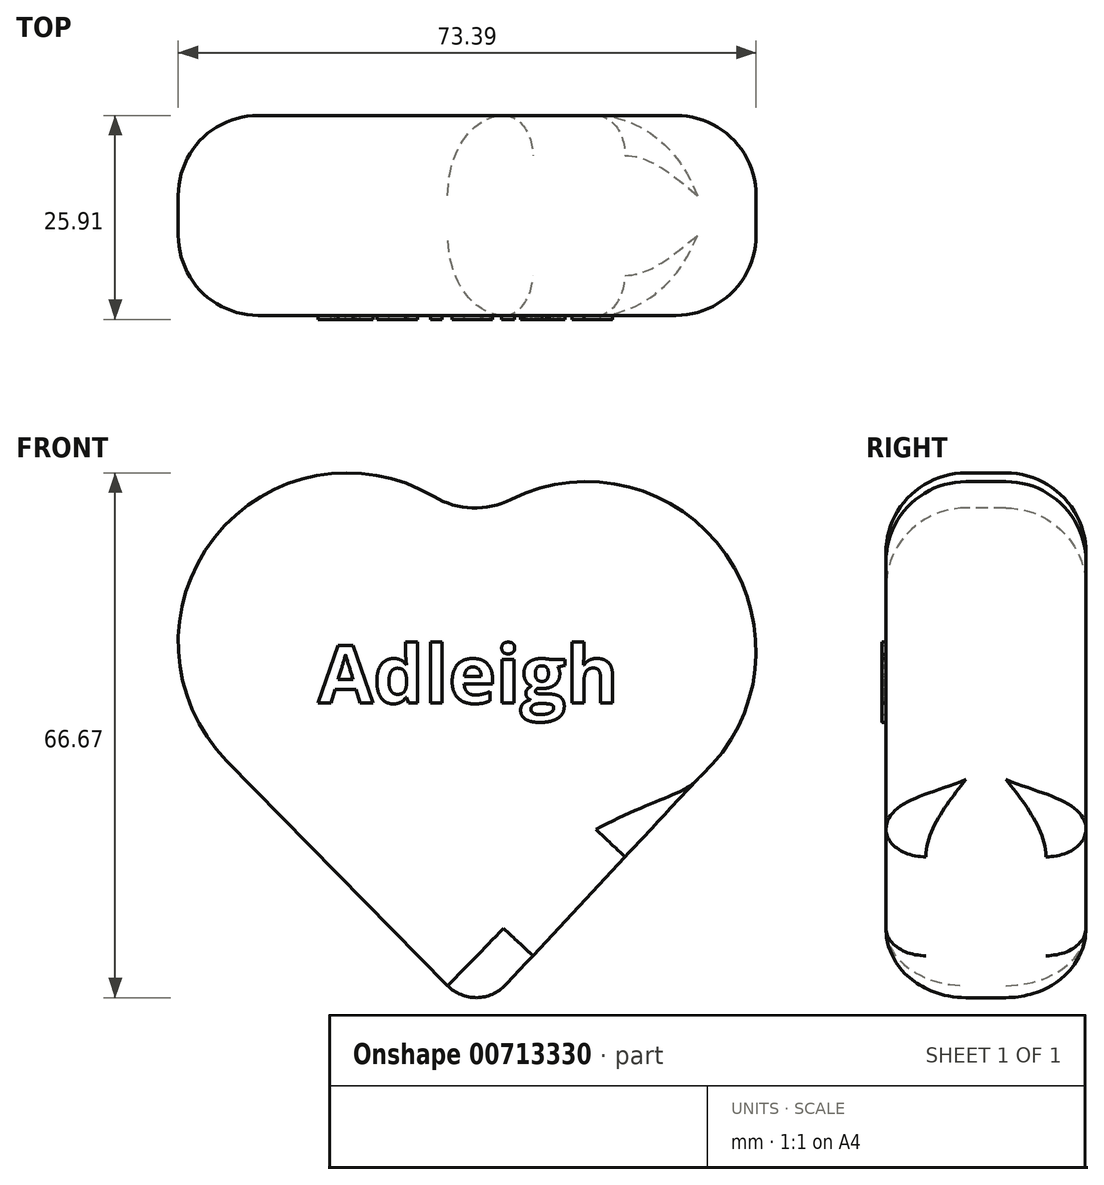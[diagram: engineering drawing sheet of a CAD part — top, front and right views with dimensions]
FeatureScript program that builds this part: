
annotation { "Feature Type Name" : "Feature", "Feature Type Description" : "" }
export const myFeature = defineFeature(function(context is Context, id is Id, definition is map)
    precondition{}
    {
        {
            var Q0;
            Q0=qCreatedBy(makeId("Front.planeOp"),FACE);
            var sketch = newSketch(context, id + "F0", { "sketchPlane" : qUnion([Q0])});
            skArc(sketch, "E0", {"start": v(-28.69, 48.9) * mm, "mid": v(-59.42, 50.26) * mm, "end": v(-60.06, 19.5) * mm});
            skArc(sketch, "E1", {"start": v(0, 17.42) * mm, "mid": v(1.36, 48.15) * mm, "end": v(-29.4, 48.8) * mm});
            skLineSegment(sketch, "E2", {"start": v(-60.06, 19.5) * mm, "end": v(-28.28, -12.86) * mm});
            skLineSegment(sketch, "E3", {"start": v(-28.28, -12.86) * mm, "end": v(0, 17.42) * mm});
            skSolve(sketch);
        }
        {
            var Q0;
            Q0 = qSketchRegion(id + "F0", true);
            extrude(context, id + "F1", {"entities" : qUnion([Q0]), "depth" : 25.4 * mm, "offsetDistance" : 25.4 * mm});
        }
        {
            var Q0;
            Q0=makeQuery(id+"F1.opExtrude","SWEPT_FACE",FACE,{"disambiguationData":[OSD([sQuery(id+"F0.wireOp",EDGE,"E0")])]});
            var Q1;
            Q1=makeQuery(id+"F1.opExtrude","SWEPT_FACE",FACE,{"disambiguationData":[OSD([sQuery(id+"F0.wireOp",EDGE,"E1")])]});
            fillet(context, id + "F2", {"entities" : qUnion([Q0, Q1]), "radius" : 10.16 * mm, "tangentPropagation" : true, "allowEdgeOverflow" : false});
        }
        {
            var Q0;
            Q0=qCreatedBy(makeId("Front.planeOp"),FACE);
            var sketch = newSketch(context, id + "F3", { "sketchPlane" : qUnion([Q0])});
            skText(sketch, "E4", { "text": "Adleigh", "fontName": "OpenSans-Bold.ttf"});
            const initialGuessF3  = {"E4": [-0.04849, 0.02682, 1, 0, 0.00734]};
            skSetInitialGuess(sketch, initialGuessF3);
            skSolve(sketch);
        }
        {
            var Q0;
            Q0 = qSketchRegion(id + "F3", true);
            extrude(context, id + "F4", {"entities" : qUnion([Q0]), "operationType" : NewBodyOperationType.ADD, "depth" : 25.9 * mm, "offsetDistance" : 25.4 * mm});
        }
        {
            var Q0;
            Q0=makeQuery(id+"F2.opFillet","BLEND_EDGE",EDGE,{"blendedFrom":[makeQuery(id+"F1.opExtrude","CAP_EDGE",EDGE,{"disambiguationData":[OSD([sQuery(id+"F0.wireOp",EDGE,"E2")])],"isStart":false}),makeQuery(id+"F1.opExtrude","CAP_EDGE",EDGE,{"disambiguationData":[OSD([sQuery(id+"F0.wireOp",EDGE,"E3")])],"isStart":false})],"blendedInto":[]});
            var Q1;
            Q1=makeQuery(id+"F2.opFillet","BLEND_EDGE",EDGE,{"blendedFrom":[makeQuery(id+"F1.opExtrude","CAP_EDGE",EDGE,{"disambiguationData":[OSD([sQuery(id+"F0.wireOp",EDGE,"E2")])],"isStart":true}),makeQuery(id+"F1.opExtrude","CAP_EDGE",EDGE,{"disambiguationData":[OSD([sQuery(id+"F0.wireOp",EDGE,"E3")])],"isStart":true})],"blendedInto":[]});
            var Q2;
            Q2=makeQuery(id+"F1.opExtrude","SWEPT_EDGE",EDGE,{"disambiguationData":[OSD([sQuery(id+"F0.wireOp",EDGE,"E2"),sQuery(id+"F0.wireOp",EDGE,"E3")])]});
            fillet(context, id + "F5", {"entities" : qUnion([Q0, Q1, Q2]), "radius" : 5.08 * mm, "tangentPropagation" : true, "allowEdgeOverflow" : false});
        }
    });
